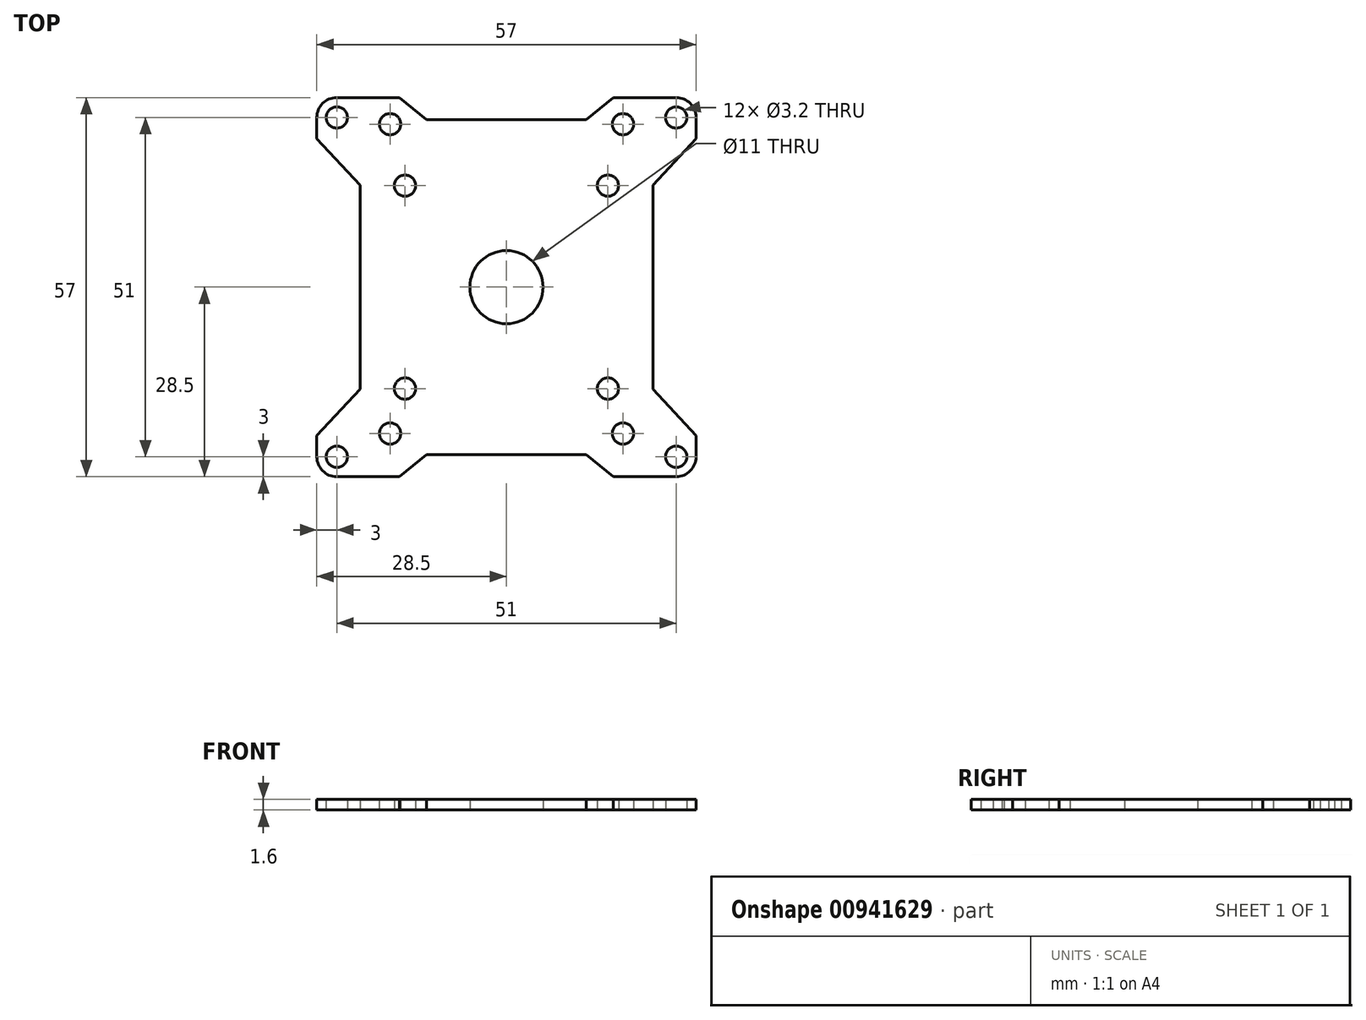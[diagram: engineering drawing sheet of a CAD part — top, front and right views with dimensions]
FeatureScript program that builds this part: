
annotation { "Feature Type Name" : "Feature", "Feature Type Description" : "" }
export const myFeature = defineFeature(function(context is Context, id is Id, definition is map)
    precondition{}
    {
        {
            var Q0;
            Q0=qCreatedBy(makeId("Top.planeOp"),FACE);
            var sketch = newSketch(context, id + "F0", { "sketchPlane" : qUnion([Q0])});
            skCircle(sketch, "E0.0", {"center": v(-17.5, -30) * mm, "radius": 1.6 * mm});
            skCircle(sketch, "E0.1", {"center": v(-17.5, 16.5) * mm, "radius": 1.6 * mm});
            skCircle(sketch, "E0.2", {"center": v(17.5, 16.5) * mm, "radius": 1.6 * mm});
            skCircle(sketch, "E0.3", {"center": v(17.5, -30) * mm, "radius": 1.6 * mm});
            skCircle(sketch, "E0.4", {"center": v(-15.25, 7.25) * mm, "radius": 1.6 * mm});
            skCircle(sketch, "E0.5", {"center": v(-15.25, -23.25) * mm, "radius": 1.6 * mm});
            skCircle(sketch, "E0.6", {"center": v(15.25, 7.25) * mm, "radius": 1.6 * mm});
            skCircle(sketch, "E0.7", {"center": v(15.25, -23.25) * mm, "radius": 1.6 * mm});
            skLineSegment(sketch, "E1", {"start": v(-15.25, 7.25) * mm, "end": v(15.25, -23.25) * mm, "construction": true});
            skLineSegment(sketch, "E2", {"start": v(-15.25, -23.25) * mm, "end": v(15.25, 7.25) * mm, "construction": true});
            skPoint(sketch, "E3", {"position": v(0, -8) * mm});
            skCircle(sketch, "E4.0", {"center": v(25.5, -33.5) * mm, "radius": 1.6 * mm});
            skCircle(sketch, "E4.1", {"center": v(-25.5, -33.5) * mm, "radius": 1.6 * mm});
            skCircle(sketch, "E4.2", {"center": v(-25.5, 17.5) * mm, "radius": 1.6 * mm});
            skPoint(sketch, "E5.visualSharp", {"position": v(-28.5, 20.5) * mm});
            skArc(sketch, "E5.filletArc", {"start": v(-25.5, 20.5) * mm, "mid": v(-27.62, 19.62) * mm, "end": v(-28.5, 17.5) * mm});
            skLineSegment(sketch, "E6", {"start": v(-25.5, 20.5) * mm, "end": v(-16.05, 20.5) * mm});
            skLineSegment(sketch, "E7", {"start": v(-16.05, 20.5) * mm, "end": v(-12, 17.2) * mm});
            skLineSegment(sketch, "E8", {"start": v(-12, 17.2) * mm, "end": v(0, 17.2) * mm});
            skLineSegment(sketch, "E9", {"start": v(-28.5, 17.5) * mm, "end": v(-28.5, 14.32) * mm});
            skLineSegment(sketch, "E10", {"start": v(-28.5, 14.32) * mm, "end": v(-22, 7.31) * mm});
            skLineSegment(sketch, "E11", {"start": v(-22, 7.31) * mm, "end": v(-22, -8) * mm});
            skLineSegment(sketch, "E12", {"start": v(0, -8) * mm, "end": v(-36.69, -8) * mm, "construction": true});
            skLineSegment(sketch, "E13.MirrorCS", {"start": v(-22, -23.31) * mm, "end": v(-22, -8) * mm});
            skLineSegment(sketch, "E14.MirrorCS", {"start": v(-28.5, -30.32) * mm, "end": v(-22, -23.31) * mm});
            skLineSegment(sketch, "E15.MirrorCS", {"start": v(-28.5, -33.5) * mm, "end": v(-28.5, -30.32) * mm});
            skArc(sketch, "E16.MirrorCS", {"start": v(-25.5, -36.5) * mm, "mid": v(-27.62, -35.62) * mm, "end": v(-28.5, -33.5) * mm});
            skLineSegment(sketch, "E17.MirrorCS", {"start": v(-25.5, -36.5) * mm, "end": v(-16.05, -36.5) * mm});
            skLineSegment(sketch, "E18.MirrorCS", {"start": v(-16.05, -36.5) * mm, "end": v(-12, -33.2) * mm});
            skLineSegment(sketch, "E19.MirrorCS", {"start": v(-12, -33.2) * mm, "end": v(0, -33.2) * mm});
            skLineSegment(sketch, "E20.MirrorCS", {"start": v(16.05, -36.5) * mm, "end": v(12, -33.2) * mm});
            skLineSegment(sketch, "E21.MirrorCS", {"start": v(25.5, -36.5) * mm, "end": v(16.05, -36.5) * mm});
            skArc(sketch, "E22.MirrorCS", {"start": v(25.5, -36.5) * mm, "mid": v(27.62, -35.62) * mm, "end": v(28.5, -33.5) * mm});
            skLineSegment(sketch, "E23.MirrorCS", {"start": v(28.5, -33.5) * mm, "end": v(28.5, -30.32) * mm});
            skLineSegment(sketch, "E24.MirrorCS", {"start": v(28.5, -30.32) * mm, "end": v(22, -23.31) * mm});
            skLineSegment(sketch, "E25.MirrorCS", {"start": v(22, -23.31) * mm, "end": v(22, -8) * mm});
            skLineSegment(sketch, "E26.MirrorCS", {"start": v(22, 7.31) * mm, "end": v(22, -8) * mm});
            skLineSegment(sketch, "E27.MirrorCS", {"start": v(28.5, 14.32) * mm, "end": v(22, 7.31) * mm});
            skLineSegment(sketch, "E28.MirrorCS", {"start": v(28.5, 17.5) * mm, "end": v(28.5, 14.32) * mm});
            skArc(sketch, "E29.MirrorCS", {"start": v(25.5, 20.5) * mm, "mid": v(27.62, 19.62) * mm, "end": v(28.5, 17.5) * mm});
            skLineSegment(sketch, "E30.MirrorCS", {"start": v(25.5, 20.5) * mm, "end": v(16.05, 20.5) * mm});
            skLineSegment(sketch, "E31.MirrorCS", {"start": v(16.05, 20.5) * mm, "end": v(12, 17.2) * mm});
            skLineSegment(sketch, "E32.MirrorCS", {"start": v(12, -33.2) * mm, "end": v(0, -33.2) * mm});
            skLineSegment(sketch, "E33.MirrorCS", {"start": v(12, 17.2) * mm, "end": v(0, 17.2) * mm});
            skCircle(sketch, "E34.0", {"center": v(0, -8) * mm, "radius": 5.5 * mm});
            skCircle(sketch, "E35.0", {"center": v(25.5, 17.5) * mm, "radius": 1.6 * mm});
            skSolve(sketch);
        }
        {
            var Q0;
            Q0 = qSketchRegion(id + "F0", true);
            extrude(context, id + "F1", {"entities" : qUnion([Q0]), "depth" : 1.6 * mm, "offsetDistance" : 25 * mm});
        }
    });
